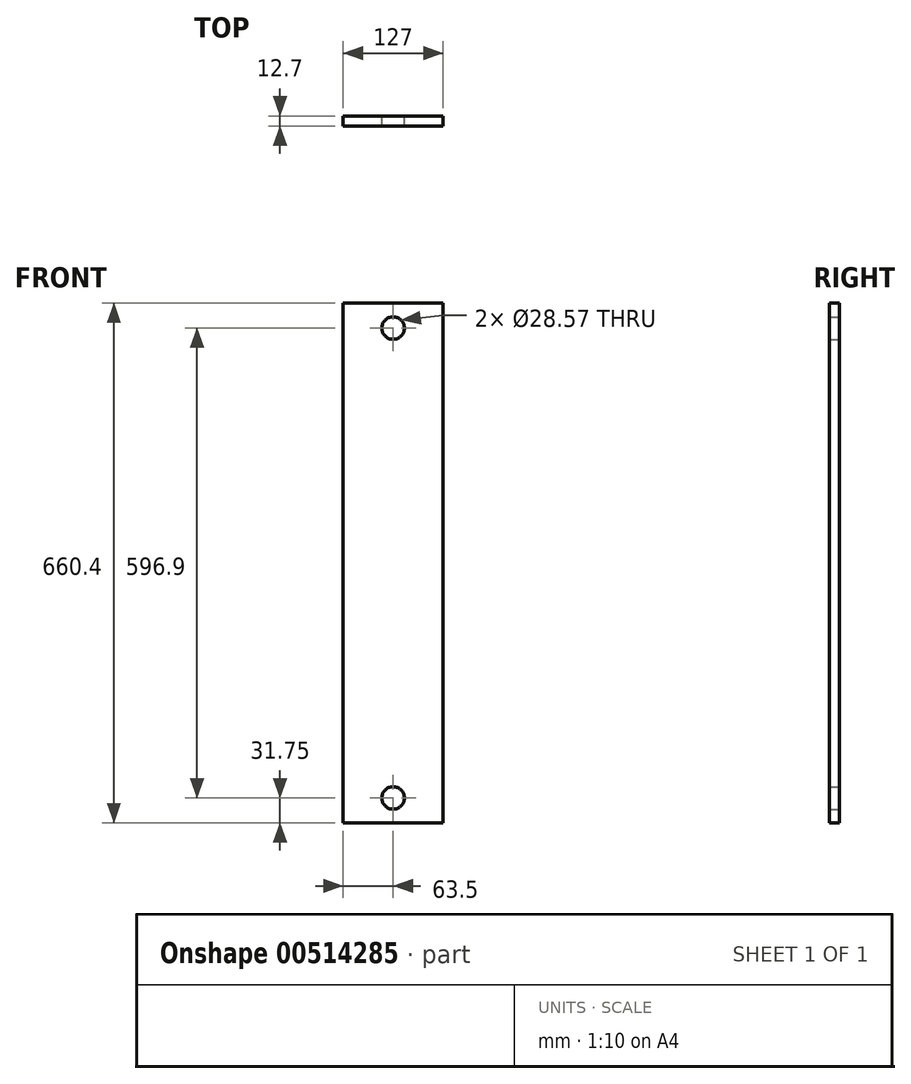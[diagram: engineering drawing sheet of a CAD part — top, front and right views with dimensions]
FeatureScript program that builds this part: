
annotation { "Feature Type Name" : "Feature", "Feature Type Description" : "" }
export const myFeature = defineFeature(function(context is Context, id is Id, definition is map)
    precondition{}
    {
        {
            var Q0;
            Q0=qCreatedBy(makeId("Front.planeOp"),FACE);
            var sketch = newSketch(context, id + "F0", { "sketchPlane" : qUnion([Q0])});
            skLineSegment(sketch, "E0.bottom", {"start": v(63.5, -330.2) * mm, "end": v(-63.5, -330.2) * mm});
            skLineSegment(sketch, "E0.top", {"start": v(63.5, 330.2) * mm, "end": v(-63.5, 330.2) * mm});
            skLineSegment(sketch, "E0.left", {"start": v(63.5, -330.2) * mm, "end": v(63.5, 330.2) * mm});
            skLineSegment(sketch, "E0.right", {"start": v(-63.5, -330.2) * mm, "end": v(-63.5, 330.2) * mm});
            skPoint(sketch, "E0.middle", {"position": v(0, 0) * mm});
            skCircle(sketch, "E1", {"center": v(0, 298.45) * mm, "radius": 14.29 * mm});
            skCircle(sketch, "E2.MirrorC", {"center": v(0, -298.45) * mm, "radius": 14.29 * mm});
            skSolve(sketch);
        }
        {
            var Q0;
            Q0 = qSketchRegion(id + "F0", true);
            extrude(context, id + "F1", {"entities" : qUnion([Q0]), "depth" : 9.52 * mm});
        }
        {
            var Q0;
            Q0 = qSketchRegion(id + "F0", true);
            extrude(context, id + "F2", {"entities" : qUnion([Q0]), "operationType" : NewBodyOperationType.ADD, "depth" : 12.7 * mm});
        }
    });
